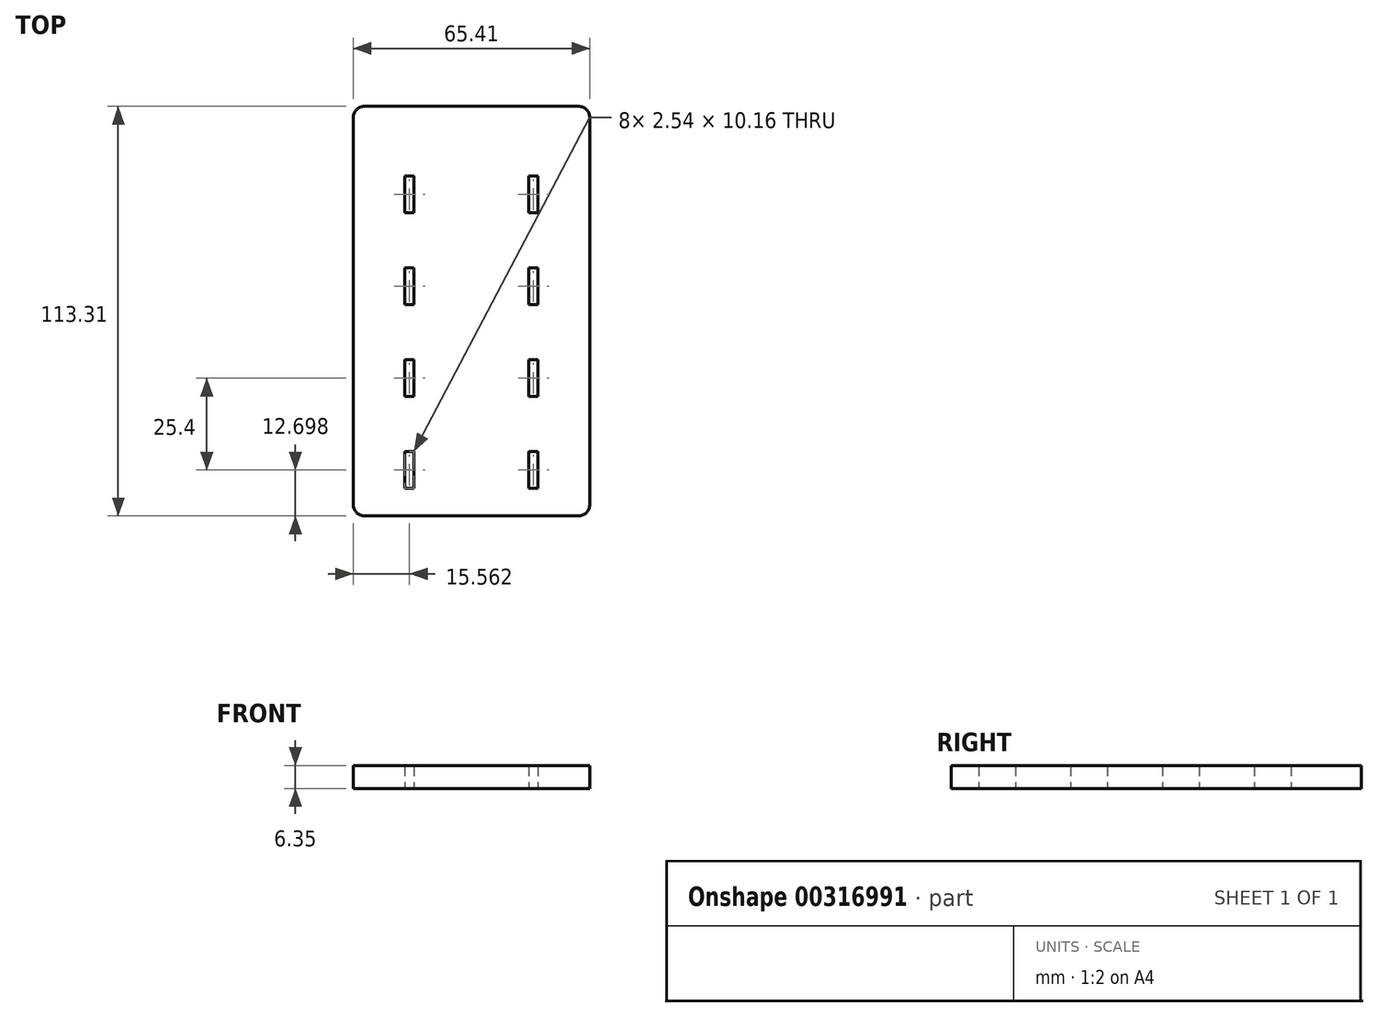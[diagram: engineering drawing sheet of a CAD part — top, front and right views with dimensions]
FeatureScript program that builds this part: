
annotation { "Feature Type Name" : "Feature", "Feature Type Description" : "" }
export const myFeature = defineFeature(function(context is Context, id is Id, definition is map)
    precondition{}
    {
        {
            var Q0;
            Q0=qCreatedBy(makeId("Top.planeOp"),FACE);
            var sketch = newSketch(context, id + "F0", { "sketchPlane" : qUnion([Q0])});
            skLineSegment(sketch, "E0.bottom", {"start": v(-33.67, 44.6) * mm, "end": v(25.38, 44.6) * mm});
            skLineSegment(sketch, "E0.top", {"start": v(-33.67, 157.9) * mm, "end": v(25.38, 157.9) * mm});
            skLineSegment(sketch, "E0.left", {"start": v(-36.85, 47.77) * mm, "end": v(-36.85, 154.73) * mm});
            skLineSegment(sketch, "E0.right", {"start": v(28.56, 47.77) * mm, "end": v(28.56, 154.73) * mm});
            skPoint(sketch, "E1.visualSharp", {"position": v(-36.85, 44.6) * mm});
            skArc(sketch, "E1.filletArc", {"start": v(-36.85, 47.77) * mm, "mid": v(-35.92, 45.53) * mm, "end": v(-33.67, 44.6) * mm});
            skPoint(sketch, "E2.visualSharp", {"position": v(28.56, 44.6) * mm});
            skArc(sketch, "E2.filletArc", {"start": v(25.38, 44.6) * mm, "mid": v(27.63, 45.53) * mm, "end": v(28.56, 47.77) * mm});
            skPoint(sketch, "E3.visualSharp", {"position": v(28.56, 157.9) * mm});
            skArc(sketch, "E3.filletArc", {"start": v(28.56, 154.73) * mm, "mid": v(27.63, 156.98) * mm, "end": v(25.38, 157.9) * mm});
            skPoint(sketch, "E4.visualSharp", {"position": v(-36.85, 157.9) * mm});
            skArc(sketch, "E4.filletArc", {"start": v(-33.67, 157.9) * mm, "mid": v(-35.92, 156.98) * mm, "end": v(-36.85, 154.73) * mm});
            skLineSegment(sketch, "E5.bottom", {"start": v(-22.56, 62.38) * mm, "end": v(-20.02, 62.38) * mm});
            skLineSegment(sketch, "E5.top", {"start": v(-22.56, 52.22) * mm, "end": v(-20.02, 52.22) * mm});
            skLineSegment(sketch, "E5.left", {"start": v(-22.56, 62.38) * mm, "end": v(-22.56, 52.22) * mm});
            skLineSegment(sketch, "E5.right", {"start": v(-20.02, 62.38) * mm, "end": v(-20.02, 52.22) * mm});
            skLineSegment(sketch, "E6.0.1.0", {"start": v(-20.02, 87.78) * mm, "end": v(-20.02, 77.62) * mm});
            skLineSegment(sketch, "E6.0.1.1", {"start": v(-22.56, 87.78) * mm, "end": v(-20.02, 87.78) * mm});
            skLineSegment(sketch, "E6.0.1.2", {"start": v(-22.56, 77.62) * mm, "end": v(-20.02, 77.62) * mm});
            skLineSegment(sketch, "E6.0.1.3", {"start": v(-22.56, 87.78) * mm, "end": v(-22.56, 77.62) * mm});
            skLineSegment(sketch, "E6.0.2.0", {"start": v(-20.02, 113.18) * mm, "end": v(-20.02, 103.02) * mm});
            skLineSegment(sketch, "E6.0.2.1", {"start": v(-22.56, 113.18) * mm, "end": v(-20.02, 113.18) * mm});
            skLineSegment(sketch, "E6.0.2.2", {"start": v(-22.56, 103.02) * mm, "end": v(-20.02, 103.02) * mm});
            skLineSegment(sketch, "E6.0.2.3", {"start": v(-22.56, 113.18) * mm, "end": v(-22.56, 103.02) * mm});
            skLineSegment(sketch, "E6.0.3.0", {"start": v(-20.02, 138.58) * mm, "end": v(-20.02, 128.42) * mm});
            skLineSegment(sketch, "E6.0.3.1", {"start": v(-22.56, 138.58) * mm, "end": v(-20.02, 138.58) * mm});
            skLineSegment(sketch, "E6.0.3.2", {"start": v(-22.56, 128.42) * mm, "end": v(-20.02, 128.42) * mm});
            skLineSegment(sketch, "E6.0.3.3", {"start": v(-22.56, 138.58) * mm, "end": v(-22.56, 128.42) * mm});
            skLineSegment(sketch, "E6.1.0.0", {"start": v(14.27, 62.38) * mm, "end": v(14.27, 52.22) * mm});
            skLineSegment(sketch, "E6.1.0.1", {"start": v(11.73, 62.38) * mm, "end": v(14.27, 62.38) * mm});
            skLineSegment(sketch, "E6.1.0.2", {"start": v(11.73, 52.22) * mm, "end": v(14.27, 52.22) * mm});
            skLineSegment(sketch, "E6.1.0.3", {"start": v(11.73, 62.38) * mm, "end": v(11.73, 52.22) * mm});
            skLineSegment(sketch, "E6.1.1.0", {"start": v(14.27, 87.78) * mm, "end": v(14.27, 77.62) * mm});
            skLineSegment(sketch, "E6.1.1.1", {"start": v(11.73, 87.78) * mm, "end": v(14.27, 87.78) * mm});
            skLineSegment(sketch, "E6.1.1.2", {"start": v(11.73, 77.62) * mm, "end": v(14.27, 77.62) * mm});
            skLineSegment(sketch, "E6.1.1.3", {"start": v(11.73, 87.78) * mm, "end": v(11.73, 77.62) * mm});
            skLineSegment(sketch, "E6.1.2.0", {"start": v(14.27, 113.18) * mm, "end": v(14.27, 103.02) * mm});
            skLineSegment(sketch, "E6.1.2.1", {"start": v(11.73, 113.18) * mm, "end": v(14.27, 113.18) * mm});
            skLineSegment(sketch, "E6.1.2.2", {"start": v(11.73, 103.02) * mm, "end": v(14.27, 103.02) * mm});
            skLineSegment(sketch, "E6.1.2.3", {"start": v(11.73, 113.18) * mm, "end": v(11.73, 103.02) * mm});
            skLineSegment(sketch, "E6.1.3.0", {"start": v(14.27, 138.58) * mm, "end": v(14.27, 128.42) * mm});
            skLineSegment(sketch, "E6.1.3.1", {"start": v(11.73, 138.58) * mm, "end": v(14.27, 138.58) * mm});
            skLineSegment(sketch, "E6.1.3.2", {"start": v(11.73, 128.42) * mm, "end": v(14.27, 128.42) * mm});
            skLineSegment(sketch, "E6.1.3.3", {"start": v(11.73, 138.58) * mm, "end": v(11.73, 128.42) * mm});
            skLineSegment(sketch, "E6.direction1", {"start": v(-22.56, 52.22) * mm, "end": v(11.73, 52.22) * mm, "construction": true});
            skLineSegment(sketch, "E6.direction2", {"start": v(-22.56, 52.22) * mm, "end": v(-22.56, 77.62) * mm, "construction": true});
            skSolve(sketch);
        }
        {
            var Q0;
            Q0=makeQuery(id+"F0.imprint","IMPRINT",FACE,{"disambiguationData":[TD([[makeQuery(id+"F0.imprint","IMPRINT",EDGE,{"derivedFrom":sQuery(id+"F0.wireOp",EDGE,"E0.bottom")}),1.0]])]});
            extrude(context, id + "F1", {"entities" : qUnion([Q0]), "depth" : 6.35 * mm});
        }
    });
